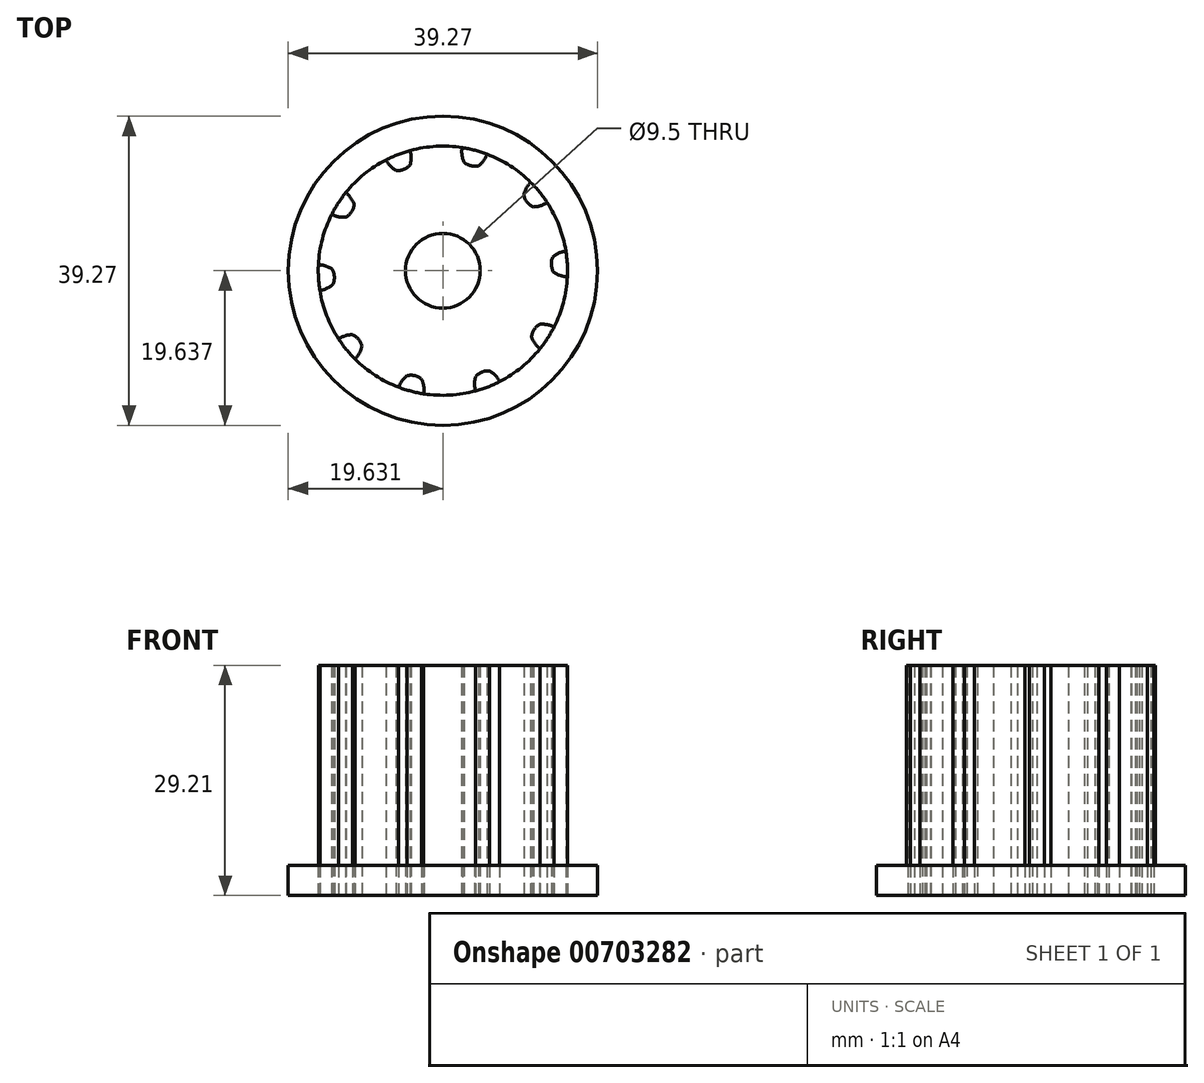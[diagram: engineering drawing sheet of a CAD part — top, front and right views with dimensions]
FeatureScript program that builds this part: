
annotation { "Feature Type Name" : "Feature", "Feature Type Description" : "" }
export const myFeature = defineFeature(function(context is Context, id is Id, definition is map)
    precondition{}
    {
        {
            var Q0;
            Q0=qCreatedBy(makeId("Top.planeOp"),FACE);
            var sketch = newSketch(context, id + "F0", { "sketchPlane" : qUnion([Q0])});
            skCircle(sketch, "E0", {"center": v(-16.76, -26.1) * mm, "radius": 4.75 * mm});
            skLineSegment(sketch, "E1", {"start": v(-22.46, -11.39) * mm, "end": v(-21.72, -13.21) * mm});
            skArc(sketch, "E2", {"start": v(-23.96, -12.05) * mm, "mid": v(-23.42, -12.8) * mm, "end": v(-22.7, -13.36) * mm});
            skArc(sketch, "E3.MirrorCS", {"start": v(-20.91, -10.82) * mm, "mid": v(-20.78, -11.74) * mm, "end": v(-20.92, -12.65) * mm});
            skArc(sketch, "E4", {"start": v(-22.7, -13.36) * mm, "mid": v(-21.72, -13.21) * mm, "end": v(-20.92, -12.65) * mm});
            skArc(sketch, "E5.1.0", {"start": v(-29.1, -16.18) * mm, "mid": v(-28.45, -16.84) * mm, "end": v(-28.03, -17.66) * mm});
            skArc(sketch, "E5.1.1", {"start": v(-29.04, -19.28) * mm, "mid": v(-28.35, -18.6) * mm, "end": v(-28.03, -17.66) * mm});
            skArc(sketch, "E5.1.2", {"start": v(-30.84, -18.96) * mm, "mid": v(-29.97, -19.25) * mm, "end": v(-29.04, -19.28) * mm});
            skArc(sketch, "E5.2.0", {"start": v(-32.57, -25.33) * mm, "mid": v(-31.66, -25.49) * mm, "end": v(-30.83, -25.9) * mm});
            skArc(sketch, "E5.2.1", {"start": v(-30.7, -27.8) * mm, "mid": v(-30.54, -26.83) * mm, "end": v(-30.83, -25.9) * mm});
            skArc(sketch, "E5.2.2", {"start": v(-32.34, -28.6) * mm, "mid": v(-31.47, -28.32) * mm, "end": v(-30.7, -27.8) * mm});
            skArc(sketch, "E5.3.0", {"start": v(-30, -34.76) * mm, "mid": v(-29.17, -34.36) * mm, "end": v(-28.26, -34.2) * mm});
            skArc(sketch, "E5.3.1", {"start": v(-27.04, -35.67) * mm, "mid": v(-27.47, -34.8) * mm, "end": v(-28.26, -34.2) * mm});
            skArc(sketch, "E5.3.2", {"start": v(-27.9, -37.28) * mm, "mid": v(-27.35, -36.54) * mm, "end": v(-27.04, -35.67) * mm});
            skArc(sketch, "E5.4.0", {"start": v(-22.37, -40.89) * mm, "mid": v(-21.94, -40.07) * mm, "end": v(-21.3, -39.42) * mm});
            skArc(sketch, "E5.4.1", {"start": v(-19.44, -39.88) * mm, "mid": v(-20.31, -39.43) * mm, "end": v(-21.3, -39.42) * mm});
            skArc(sketch, "E5.4.2", {"start": v(-19.19, -41.7) * mm, "mid": v(-19.18, -40.77) * mm, "end": v(-19.44, -39.88) * mm});
            skArc(sketch, "E5.5.0", {"start": v(-12.6, -41.36) * mm, "mid": v(-12.73, -40.45) * mm, "end": v(-12.6, -39.54) * mm});
            skArc(sketch, "E5.5.1", {"start": v(-10.82, -38.83) * mm, "mid": v(-11.8, -38.97) * mm, "end": v(-12.6, -39.54) * mm});
            skArc(sketch, "E5.5.2", {"start": v(-9.56, -40.14) * mm, "mid": v(-10.1, -39.4) * mm, "end": v(-10.82, -38.83) * mm});
            skArc(sketch, "E5.6.0", {"start": v(-4.42, -36) * mm, "mid": v(-5.06, -35.34) * mm, "end": v(-5.49, -34.52) * mm});
            skArc(sketch, "E5.6.1", {"start": v(-4.47, -32.9) * mm, "mid": v(-5.17, -33.6) * mm, "end": v(-5.49, -34.52) * mm});
            skArc(sketch, "E5.6.2", {"start": v(-2.67, -33.22) * mm, "mid": v(-3.55, -32.94) * mm, "end": v(-4.47, -32.9) * mm});
            skArc(sketch, "E5.7.0", {"start": v(-0.95, -26.86) * mm, "mid": v(-1.86, -26.7) * mm, "end": v(-2.69, -26.29) * mm});
            skArc(sketch, "E5.7.1", {"start": v(-2.81, -24.38) * mm, "mid": v(-2.97, -25.35) * mm, "end": v(-2.69, -26.29) * mm});
            skArc(sketch, "E5.7.2", {"start": v(-1.17, -23.58) * mm, "mid": v(-2.05, -23.87) * mm, "end": v(-2.81, -24.38) * mm});
            skArc(sketch, "E5.8.0", {"start": v(-3.52, -17.42) * mm, "mid": v(-4.35, -17.83) * mm, "end": v(-5.26, -17.98) * mm});
            skArc(sketch, "E5.8.1", {"start": v(-6.48, -16.52) * mm, "mid": v(-6.04, -17.4) * mm, "end": v(-5.26, -17.98) * mm});
            skArc(sketch, "E5.8.2", {"start": v(-5.62, -14.9) * mm, "mid": v(-6.17, -15.65) * mm, "end": v(-6.48, -16.52) * mm});
            skArc(sketch, "E5.9.0", {"start": v(-11.14, -11.3) * mm, "mid": v(-11.58, -12.11) * mm, "end": v(-12.22, -12.77) * mm});
            skArc(sketch, "E5.9.1", {"start": v(-14.07, -12.3) * mm, "mid": v(-13.2, -12.76) * mm, "end": v(-12.22, -12.77) * mm});
            skArc(sketch, "E5.9.2", {"start": v(-14.33, -10.5) * mm, "mid": v(-14.33, -11.42) * mm, "end": v(-14.07, -12.3) * mm});
            skCircle(sketch, "E6", {"center": v(-16.76, -26.1) * mm, "radius": 15.83 * mm});
            skCircle(sketch, "E7", {"center": v(-16.76, -26.1) * mm, "radius": 12.02 * mm});
            skLineSegment(sketch, "E8", {"start": v(-32.34, -28.6) * mm, "end": v(-32.38, -28.6) * mm});
            skLineSegment(sketch, "E9", {"start": v(-27.9, -37.28) * mm, "end": v(-27.94, -37.33) * mm});
            skLineSegment(sketch, "E10", {"start": v(-19.19, -41.7) * mm, "end": v(-19.19, -41.73) * mm});
            skLineSegment(sketch, "E11", {"start": v(-9.56, -40.14) * mm, "end": v(-9.54, -40.18) * mm});
            skLineSegment(sketch, "E12", {"start": v(-2.67, -33.22) * mm, "end": v(-2.64, -33.24) * mm});
            skLineSegment(sketch, "E13", {"start": v(-1.17, -23.58) * mm, "end": v(-1.1, -23.57) * mm});
            skLineSegment(sketch, "E14", {"start": v(-5.62, -14.9) * mm, "end": v(-5.6, -14.87) * mm});
            skLineSegment(sketch, "E15", {"start": v(-14.33, -10.5) * mm, "end": v(-14.28, -10.46) * mm});
            skLineSegment(sketch, "E16", {"start": v(-23.96, -12.05) * mm, "end": v(-24, -11.98) * mm});
            skLineSegment(sketch, "E17", {"start": v(-30.84, -18.96) * mm, "end": v(-30.88, -18.94) * mm});
            skCircle(sketch, "E18", {"center": v(-16.76, -26.1) * mm, "radius": 19.64 * mm});
            skSolve(sketch);
        }
        {
            var Q0;
            Q0=makeQuery(id+"F0.imprint","IMPRINT",FACE,{"disambiguationData":[TD([[makeQuery(id+"F0.imprint","IMPRINT",EDGE,{"derivedFrom":sQuery(id+"F0.wireOp",EDGE,"E0")}),-1.0]])]});
            var Q1;
            {var subQ25=sQuery(id+"F0.wireOp",EDGE,"E2");Q1=makeQuery(id+"F0.imprint","IMPRINT",FACE,{"disambiguationData":[TD([[makeQuery(id+"F0.imprint","IMPRINT",EDGE,{"derivedFrom":subQ25}),-1.0]])]});}
            var Q2;
            Q2=makeQuery(id+"F0.imprint","IMPRINT",FACE,{"disambiguationData":[TD([[makeQuery(id+"F0.imprint","IMPRINT",EDGE,{"derivedFrom":sQuery(id+"F0.wireOp",EDGE,"E18")}),1.0]])]});
            extrude(context, id + "F1", {"entities" : qUnion([Q0, Q1, Q2]), "depth" : 3.8 * mm, "offsetDistance" : 25.4 * mm});
        }
        {
            var Q0;
            Q0=makeQuery(id+"F0.imprint","IMPRINT",FACE,{"disambiguationData":[TD([[makeQuery(id+"F0.imprint","IMPRINT",EDGE,{"derivedFrom":sQuery(id+"F0.wireOp",EDGE,"E0")}),-1.0]])]});
            var Q1;
            {var subQ25=sQuery(id+"F0.wireOp",EDGE,"E2");Q1=makeQuery(id+"F0.imprint","IMPRINT",FACE,{"disambiguationData":[TD([[makeQuery(id+"F0.imprint","IMPRINT",EDGE,{"derivedFrom":subQ25}),-1.0]])]});}
            extrude(context, id + "F2", {"entities" : qUnion([Q0, Q1]), "operationType" : NewBodyOperationType.ADD, "depth" : 29.2 * mm, "offsetDistance" : 25.4 * mm});
        }
    });
